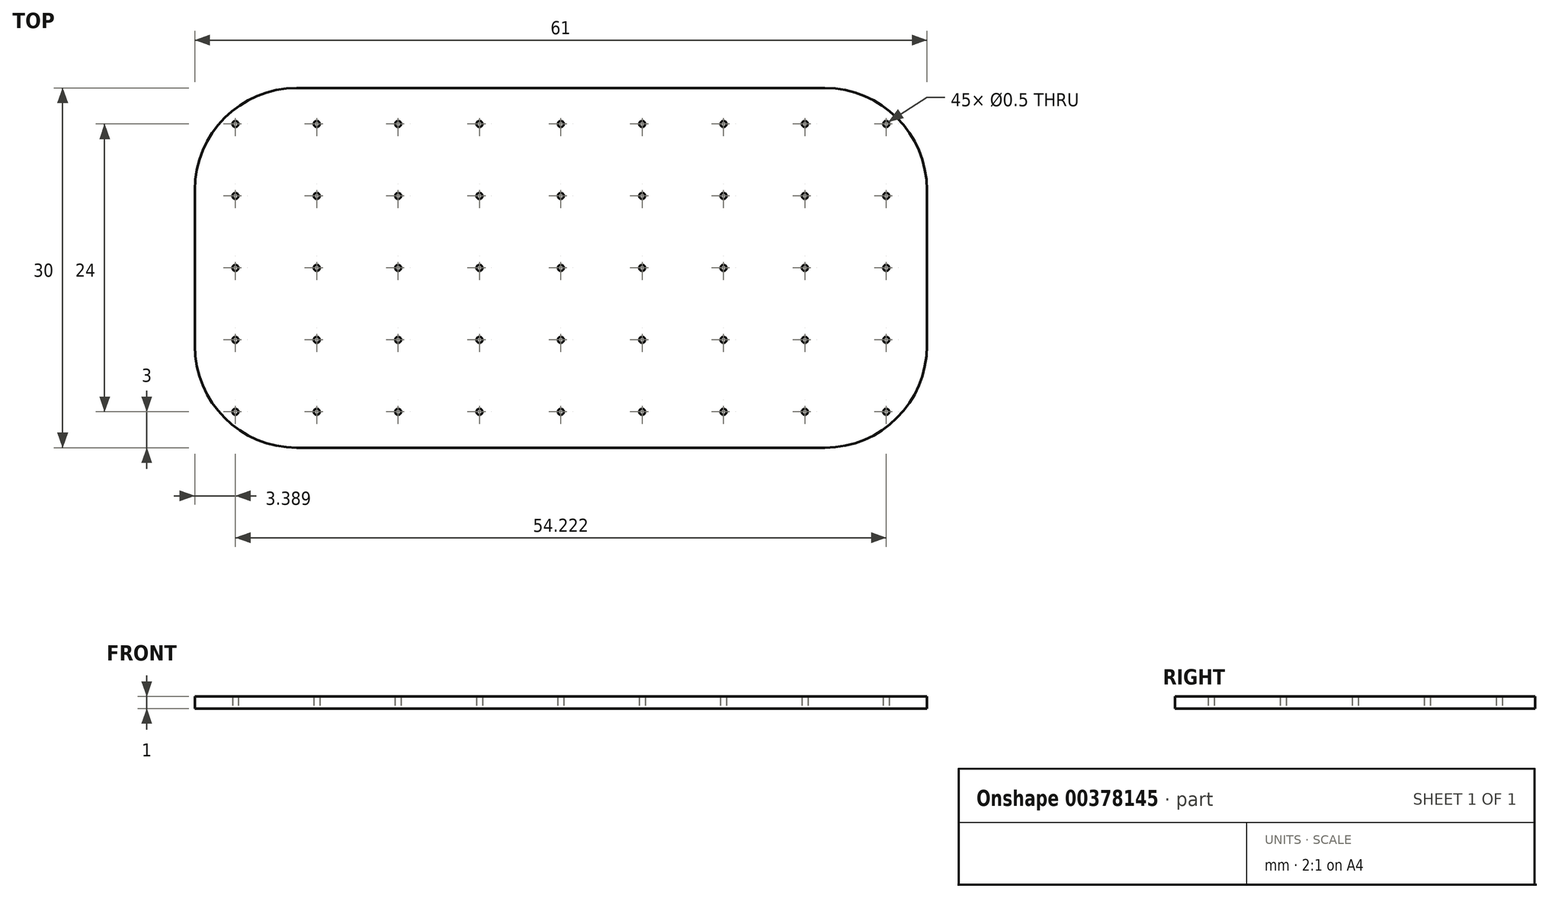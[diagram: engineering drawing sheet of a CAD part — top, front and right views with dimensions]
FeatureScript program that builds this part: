
annotation { "Feature Type Name" : "Feature", "Feature Type Description" : "" }
export const myFeature = defineFeature(function(context is Context, id is Id, definition is map)
    precondition{}
    {
        {
            var Q0;
            Q0=qCreatedBy(makeId("Top.planeOp"),FACE);
            var sketch = newSketch(context, id + "F0", { "sketchPlane" : qUnion([Q0])});
            skLineSegment(sketch, "E0.bottom", {"start": v(22, 15) * mm, "end": v(-22, 15) * mm});
            skLineSegment(sketch, "E0.top", {"start": v(22, -15) * mm, "end": v(-22, -15) * mm});
            skLineSegment(sketch, "E0.left", {"start": v(30.5, 6.5) * mm, "end": v(30.5, -6.5) * mm});
            skLineSegment(sketch, "E0.right", {"start": v(-30.5, 6.5) * mm, "end": v(-30.5, -6.5) * mm});
            skPoint(sketch, "E0.middle", {"position": v(0, 0) * mm});
            skPoint(sketch, "E1.visualSharp", {"position": v(-30.5, 15) * mm});
            skArc(sketch, "E1.filletArc", {"start": v(-22, 15) * mm, "mid": v(-28.01, 12.51) * mm, "end": v(-30.5, 6.5) * mm});
            skPoint(sketch, "E2.visualSharp", {"position": v(-30.5, -15) * mm});
            skArc(sketch, "E2.filletArc", {"start": v(-30.5, -6.5) * mm, "mid": v(-28.01, -12.51) * mm, "end": v(-22, -15) * mm});
            skPoint(sketch, "E3.visualSharp", {"position": v(30.5, 15) * mm});
            skArc(sketch, "E3.filletArc", {"start": v(30.5, 6.5) * mm, "mid": v(28.01, 12.51) * mm, "end": v(22, 15) * mm});
            skPoint(sketch, "E4.visualSharp", {"position": v(30.5, -15) * mm});
            skArc(sketch, "E4.filletArc", {"start": v(22, -15) * mm, "mid": v(28.01, -12.51) * mm, "end": v(30.5, -6.5) * mm});
            skSolve(sketch);
        }
        {
            var Q0;
            Q0=makeQuery(id+"F0.imprint","IMPRINT",FACE,{"disambiguationData":[TD([[makeQuery(id+"F0.imprint","IMPRINT",EDGE,{"derivedFrom":sQuery(id+"F0.wireOp",EDGE,"E0.bottom")}),1.0]])]});
            var sketch = newSketch(context, id + "F1", { "sketchPlane" : qUnion([Q0])});
            skCircle(sketch, "E5", {"center": v(-27.11, 12) * mm, "radius": 0.25 * mm});
            skCircle(sketch, "E6.0.1.0", {"center": v(-27.11, 6) * mm, "radius": 0.25 * mm});
            skCircle(sketch, "E6.0.2.0", {"center": v(-27.11, 0) * mm, "radius": 0.25 * mm});
            skCircle(sketch, "E6.0.3.0", {"center": v(-27.11, -6) * mm, "radius": 0.25 * mm});
            skCircle(sketch, "E6.0.4.0", {"center": v(-27.11, -12) * mm, "radius": 0.25 * mm});
            skCircle(sketch, "E6.1.0.0", {"center": v(-20.33, 12) * mm, "radius": 0.25 * mm});
            skCircle(sketch, "E6.1.1.0", {"center": v(-20.33, 6) * mm, "radius": 0.25 * mm});
            skCircle(sketch, "E6.1.2.0", {"center": v(-20.33, 0) * mm, "radius": 0.25 * mm});
            skCircle(sketch, "E6.1.3.0", {"center": v(-20.33, -6) * mm, "radius": 0.25 * mm});
            skCircle(sketch, "E6.1.4.0", {"center": v(-20.33, -12) * mm, "radius": 0.25 * mm});
            skCircle(sketch, "E6.2.0.0", {"center": v(-13.56, 12) * mm, "radius": 0.25 * mm});
            skCircle(sketch, "E6.2.1.0", {"center": v(-13.56, 6) * mm, "radius": 0.25 * mm});
            skCircle(sketch, "E6.2.2.0", {"center": v(-13.56, 0) * mm, "radius": 0.25 * mm});
            skCircle(sketch, "E6.2.3.0", {"center": v(-13.56, -6) * mm, "radius": 0.25 * mm});
            skCircle(sketch, "E6.2.4.0", {"center": v(-13.56, -12) * mm, "radius": 0.25 * mm});
            skCircle(sketch, "E6.3.0.0", {"center": v(-6.78, 12) * mm, "radius": 0.25 * mm});
            skCircle(sketch, "E6.3.1.0", {"center": v(-6.78, 6) * mm, "radius": 0.25 * mm});
            skCircle(sketch, "E6.3.2.0", {"center": v(-6.78, 0) * mm, "radius": 0.25 * mm});
            skCircle(sketch, "E6.3.3.0", {"center": v(-6.78, -6) * mm, "radius": 0.25 * mm});
            skCircle(sketch, "E6.3.4.0", {"center": v(-6.78, -12) * mm, "radius": 0.25 * mm});
            skCircle(sketch, "E6.4.0.0", {"center": v(0, 12) * mm, "radius": 0.25 * mm});
            skCircle(sketch, "E6.4.1.0", {"center": v(0, 6) * mm, "radius": 0.25 * mm});
            skCircle(sketch, "E6.4.2.0", {"center": v(0, 0) * mm, "radius": 0.25 * mm});
            skCircle(sketch, "E6.4.3.0", {"center": v(0, -6) * mm, "radius": 0.25 * mm});
            skCircle(sketch, "E6.4.4.0", {"center": v(0, -12) * mm, "radius": 0.25 * mm});
            skCircle(sketch, "E6.5.0.0", {"center": v(6.78, 12) * mm, "radius": 0.25 * mm});
            skCircle(sketch, "E6.5.1.0", {"center": v(6.78, 6) * mm, "radius": 0.25 * mm});
            skCircle(sketch, "E6.5.2.0", {"center": v(6.78, 0) * mm, "radius": 0.25 * mm});
            skCircle(sketch, "E6.5.3.0", {"center": v(6.78, -6) * mm, "radius": 0.25 * mm});
            skCircle(sketch, "E6.5.4.0", {"center": v(6.78, -12) * mm, "radius": 0.25 * mm});
            skCircle(sketch, "E6.6.0.0", {"center": v(13.56, 12) * mm, "radius": 0.25 * mm});
            skCircle(sketch, "E6.6.1.0", {"center": v(13.56, 6) * mm, "radius": 0.25 * mm});
            skCircle(sketch, "E6.6.2.0", {"center": v(13.56, 0) * mm, "radius": 0.25 * mm});
            skCircle(sketch, "E6.6.3.0", {"center": v(13.56, -6) * mm, "radius": 0.25 * mm});
            skCircle(sketch, "E6.6.4.0", {"center": v(13.56, -12) * mm, "radius": 0.25 * mm});
            skCircle(sketch, "E6.7.0.0", {"center": v(20.33, 12) * mm, "radius": 0.25 * mm});
            skCircle(sketch, "E6.7.1.0", {"center": v(20.33, 6) * mm, "radius": 0.25 * mm});
            skCircle(sketch, "E6.7.2.0", {"center": v(20.33, 0) * mm, "radius": 0.25 * mm});
            skCircle(sketch, "E6.7.3.0", {"center": v(20.33, -6) * mm, "radius": 0.25 * mm});
            skCircle(sketch, "E6.7.4.0", {"center": v(20.33, -12) * mm, "radius": 0.25 * mm});
            skLineSegment(sketch, "E6.direction1", {"start": v(-27.11, 12) * mm, "end": v(-20.33, 12) * mm, "construction": true});
            skLineSegment(sketch, "E6.direction2", {"start": v(-27.11, 12) * mm, "end": v(-27.11, 6) * mm, "construction": true});
            skCircle(sketch, "E7.0.8.0", {"center": v(27.11, 12) * mm, "radius": 0.25 * mm});
            skCircle(sketch, "E7.0.8.1", {"center": v(27.11, 6) * mm, "radius": 0.25 * mm});
            skCircle(sketch, "E7.0.8.2", {"center": v(27.11, 0) * mm, "radius": 0.25 * mm});
            skCircle(sketch, "E7.0.8.3", {"center": v(27.11, -6) * mm, "radius": 0.25 * mm});
            skCircle(sketch, "E7.0.8.4", {"center": v(27.11, -12) * mm, "radius": 0.25 * mm});
            skSolve(sketch);
        }
        {
            var Q0;
            Q0 = qSketchRegion(id + "F0", true);
            extrude(context, id + "F2", {"entities" : qUnion([Q0]), "depth" : 1 * mm});
        }
        {
            var Q0;
            Q0 = qSketchRegion(id + "F1", true);
            extrude(context, id + "F3", {"entities" : qUnion([Q0]), "operationType" : NewBodyOperationType.REMOVE, "depth" : 25 * mm});
        }
    });
